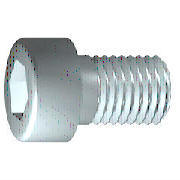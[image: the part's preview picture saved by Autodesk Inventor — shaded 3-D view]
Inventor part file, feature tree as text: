
AUTODESK INVENTOR PART (.ipt)
format: ipt  version: 2017 (Build 210142000, 142)  size: 192,512 bytes
history: native  units: mm (DEFAULTED — no unit token found)
features: sketch x2, extrude x1, plane x1, fillet x1
ambient origin geometry x7: Origin, YZ Plane, XY Plane, X Axis, Y Axis, Z Axis, Center Point
bodies: Solid1 (feature_tree), Body (feature_tree)
feature tree (5):
  extrude  "Slot"  Depth=5.0mm
  plane  "Work Plane1"
  fillet  "Fillet2"  Radius=5.0mm
  sketch  "Sketch1"  dims[d1=9.90924mm d2=0.49086mm d3=5.0mm]
  sketch  "Sketch2"  dims[d4=2.5mm d5=60.0deg d6=5.0mm d7=5.0mm d8=4.618802mm d9=8.5mm d10=90.0deg d11=10.0mm d12=0.0mm d13=9.90924mm d14=0.0mm d15=0.49076mm d16=0.49076mm d17=0.5mm d19=0.0mm d26=12.0mm d27=45.0deg d28=0.0mm d29=0.0mm d30=0.1mm]
